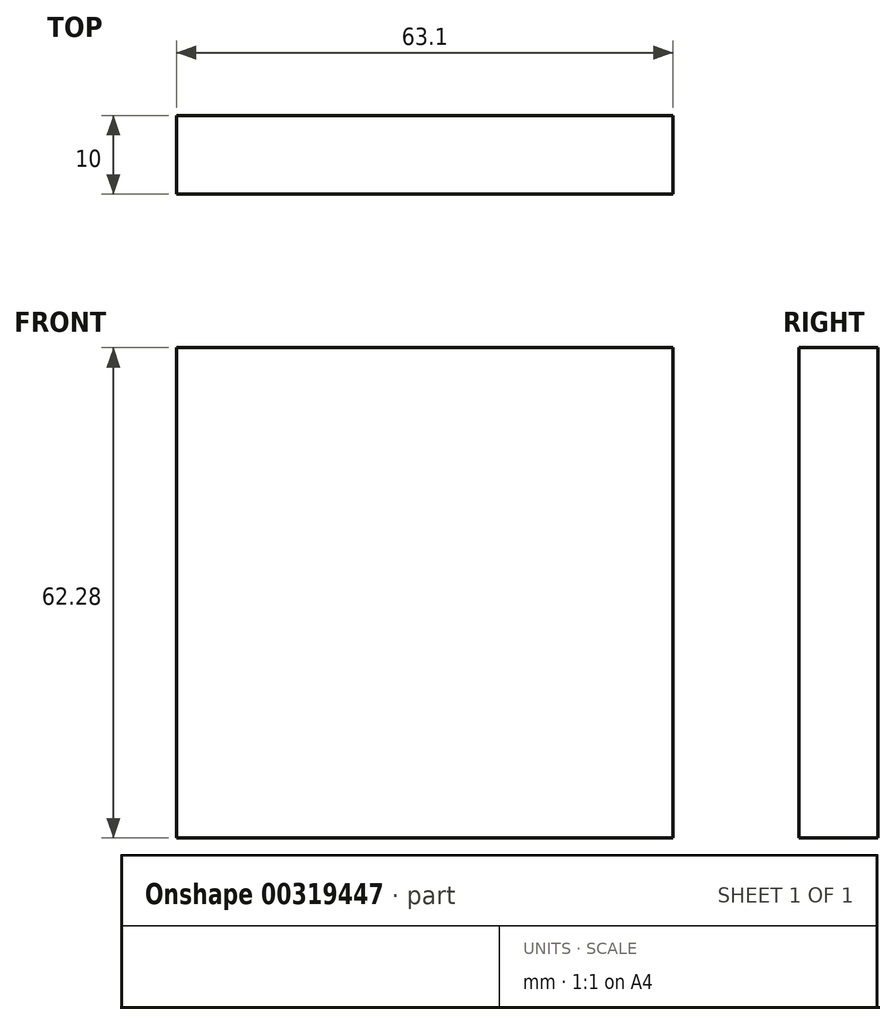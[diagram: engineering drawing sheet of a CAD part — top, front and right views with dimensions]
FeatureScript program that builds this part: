
annotation { "Feature Type Name" : "Feature", "Feature Type Description" : "" }
export const myFeature = defineFeature(function(context is Context, id is Id, definition is map)
    precondition{}
    {
        {
            var Q0;
            Q0=qCreatedBy(makeId("Front.planeOp"),FACE);
            var sketch = newSketch(context, id + "F0", { "sketchPlane" : qUnion([Q0])});
            skLineSegment(sketch, "E0.bottom", {"start": v(0, 0) * mm, "end": v(63.1, 0) * mm});
            skLineSegment(sketch, "E0.top", {"start": v(0, 62.28) * mm, "end": v(63.1, 62.28) * mm});
            skLineSegment(sketch, "E0.left", {"start": v(0, 0) * mm, "end": v(0, 62.28) * mm});
            skLineSegment(sketch, "E0.right", {"start": v(63.1, 0) * mm, "end": v(63.1, 62.28) * mm});
            skSolve(sketch);
        }
        {
            var Q0;
            Q0=makeQuery(id+"F0.imprint","IMPRINT",FACE,{"disambiguationData":[TD([[makeQuery(id+"F0.imprint","IMPRINT",EDGE,{"derivedFrom":sQuery(id+"F0.wireOp",EDGE,"E0.bottom")}),1.0]])]});
            extrude(context, id + "F1", {"entities" : qUnion([Q0]), "depth" : 10 * mm});
        }
    });
